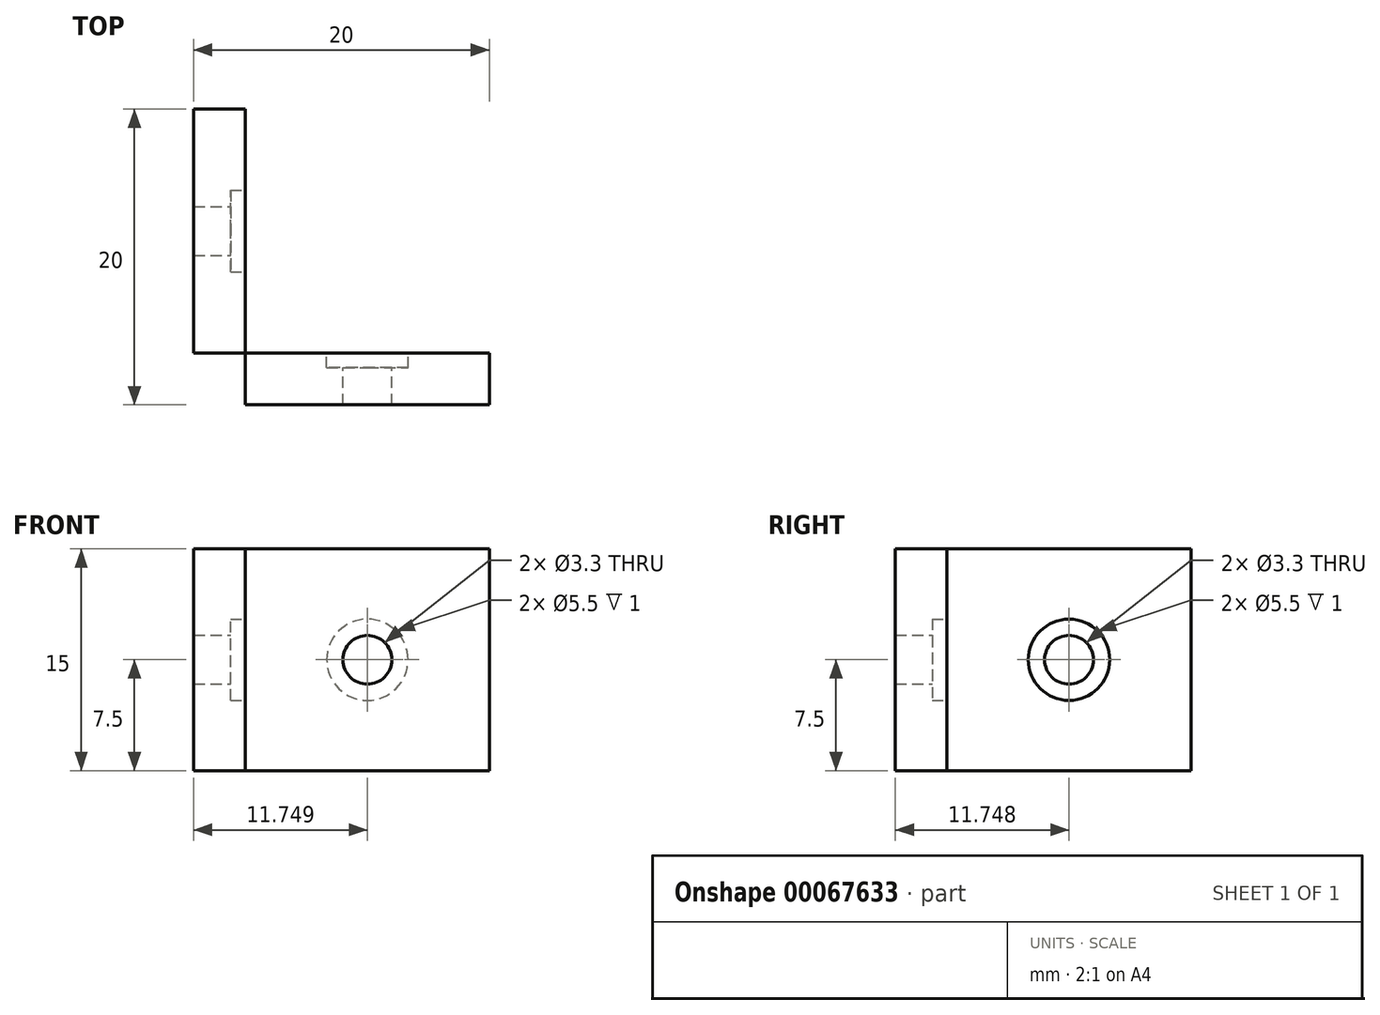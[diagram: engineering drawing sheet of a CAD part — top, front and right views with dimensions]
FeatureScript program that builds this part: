
annotation { "Feature Type Name" : "Feature", "Feature Type Description" : "" }
export const myFeature = defineFeature(function(context is Context, id is Id, definition is map)
    precondition{}
    {
        {
            var Q0;
            Q0=qCreatedBy(makeId("Top.planeOp"),FACE);
            var sketch = newSketch(context, id + "F0", { "sketchPlane" : qUnion([Q0])});
            skLineSegment(sketch, "E0.bottom", {"start": v(-12.11, 11.3) * mm, "end": v(-8.61, 11.3) * mm});
            skLineSegment(sketch, "E0.top", {"start": v(-12.11, -8.7) * mm, "end": v(-8.61, -8.7) * mm});
            skLineSegment(sketch, "E0.left", {"start": v(-12.11, 11.3) * mm, "end": v(-12.11, -8.7) * mm});
            skLineSegment(sketch, "E0.right", {"start": v(-8.61, 11.3) * mm, "end": v(-8.61, -8.7) * mm});
            skLineSegment(sketch, "E1.bottom", {"start": v(-12.11, -8.7) * mm, "end": v(7.89, -8.7) * mm});
            skLineSegment(sketch, "E1.top", {"start": v(-12.11, -5.2) * mm, "end": v(7.89, -5.2) * mm});
            skLineSegment(sketch, "E1.left", {"start": v(-12.11, -8.7) * mm, "end": v(-12.11, -5.2) * mm});
            skLineSegment(sketch, "E1.right", {"start": v(7.89, -8.7) * mm, "end": v(7.89, -5.2) * mm});
            skSolve(sketch);
        }
        {
            var Q0;
            {var subQ0=sQuery(id+"F0.wireOp",EDGE,"E0.bottom");Q0=makeQuery(id+"F0.imprint","IMPRINT",FACE,{"disambiguationData":[TD([[makeQuery(id+"F0.imprint","IMPRINT",EDGE,{"derivedFrom":subQ0}),-1.0]])]});}
            var Q1;
            {var subQ5=sQuery(id+"F0.wireOp",EDGE,"E1.left");Q1=makeQuery(id+"F0.imprint","IMPRINT",FACE,{"disambiguationData":[TD([[makeQuery(id+"F0.imprint","IMPRINT",EDGE,{"derivedFrom":subQ5}),-1.0]])]});}
            var Q2;
            {var subQ5=sQuery(id+"F0.wireOp",EDGE,"E1.right");Q2=makeQuery(id+"F0.imprint","IMPRINT",FACE,{"disambiguationData":[TD([[makeQuery(id+"F0.imprint","IMPRINT",EDGE,{"derivedFrom":subQ5}),1.0]])]});}
            extrude(context, id + "F1", {"entities" : qUnion([Q0, Q1, Q2]), "depth" : 15 * mm});
        }
        {
            var Q0;
            Q0=makeQuery(id+"F1.opExtrude","SWEPT_FACE",FACE,{"disambiguationData":[OSD([sQuery(id+"F0.wireOp",EDGE,"E0.right")])]});
            var sketch = newSketch(context, id + "F2", { "sketchPlane" : qUnion([Q0])});
            skCircle(sketch, "E2", {"center": v(3.05, 7.5) * mm, "radius": 2.75 * mm});
            skCircle(sketch, "E3", {"center": v(3.05, 7.5) * mm, "radius": 1.65 * mm});
            skSolve(sketch);
        }
        {
            var Q0;
            Q0=makeQuery(id+"F1.opExtrude","SWEPT_FACE",FACE,{"disambiguationData":[OSD([sQuery(id+"F0.wireOp",EDGE,"E1.top")])]});
            var sketch = newSketch(context, id + "F3", { "sketchPlane" : qUnion([Q0])});
            skCircle(sketch, "E4", {"center": v(0.36, 7.5) * mm, "radius": 2.75 * mm});
            skCircle(sketch, "E5", {"center": v(0.36, 7.5) * mm, "radius": 1.65 * mm});
            skSolve(sketch);
        }
        {
            var Q0;
            Q0=makeQuery(id+"F2.imprint","IMPRINT",FACE,{"disambiguationData":[TD([[makeQuery(id+"F2.imprint","IMPRINT",EDGE,{"derivedFrom":sQuery(id+"F2.wireOp",EDGE,"E3")}),1.0]])]});
            extrude(context, id + "F4", {"entities" : qUnion([Q0]), "operationType" : NewBodyOperationType.REMOVE, "endBound" : BoundingType.UP_TO_NEXT, "oppositeDirection" : true, "depth" : 25 * mm});
        }
        {
            var Q0;
            Q0=makeQuery(id+"F2.imprint","IMPRINT",FACE,{"disambiguationData":[TD([[makeQuery(id+"F2.imprint","IMPRINT",EDGE,{"derivedFrom":sQuery(id+"F2.wireOp",EDGE,"E2")}),1.0]])]});
            extrude(context, id + "F5", {"entities" : qUnion([Q0]), "operationType" : NewBodyOperationType.REMOVE, "oppositeDirection" : true, "depth" : 1 * mm});
        }
        {
            var Q0;
            Q0=makeQuery(id+"F3.imprint","IMPRINT",FACE,{"disambiguationData":[TD([[makeQuery(id+"F3.imprint","IMPRINT",EDGE,{"derivedFrom":sQuery(id+"F3.wireOp",EDGE,"E5")}),1.0]])]});
            extrude(context, id + "F6", {"entities" : qUnion([Q0]), "operationType" : NewBodyOperationType.REMOVE, "endBound" : BoundingType.UP_TO_NEXT, "oppositeDirection" : true, "depth" : mm});
        }
        {
            var Q0;
            Q0=makeQuery(id+"F3.imprint","IMPRINT",FACE,{"disambiguationData":[TD([[makeQuery(id+"F3.imprint","IMPRINT",EDGE,{"derivedFrom":sQuery(id+"F3.wireOp",EDGE,"E4")}),1.0]])]});
            extrude(context, id + "F7", {"entities" : qUnion([Q0]), "operationType" : NewBodyOperationType.REMOVE, "oppositeDirection" : true, "depth" : 1 * mm});
        }
    });
